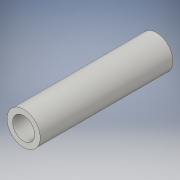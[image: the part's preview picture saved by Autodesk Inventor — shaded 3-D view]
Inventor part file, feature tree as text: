
AUTODESK INVENTOR PART (.ipt)
format: ipt  version: 2016 (Build 200138000, 138)  size: 110,080 bytes
history: native  units: in
note: dims shown in document units (in); Inventor stores cm internally (conversion verified against a paired STEP export)
features: other x2, sketch x2, extrude x1, hole x1
ambient origin geometry x8: Origin, YZ Plane, XZ Plane, XY Plane, X Axis, Y Axis, Z Axis, Center Point
bodies: Solid1 (feature_tree)
feature tree (6):
  other  "Table"
  other  "spacer-01"
  extrude  "Extrusion1"  [1 undecoded]
  hole  "Hole1"  [1 undecoded]
  sketch  "Sketch1"  dims[d2=0.0in]
  sketch  "Sketch2"  dims[d3=0.5in d4=0.75in d5=0.507in d6=0.25in d7=0.5635in d8=1.0in d9=0.8108in]
note: 2 required parameter values undecoded (feature->parameter linkage not recoverable at this tier; creation-order binding heuristic only, values carry confidence <= 0.55)
